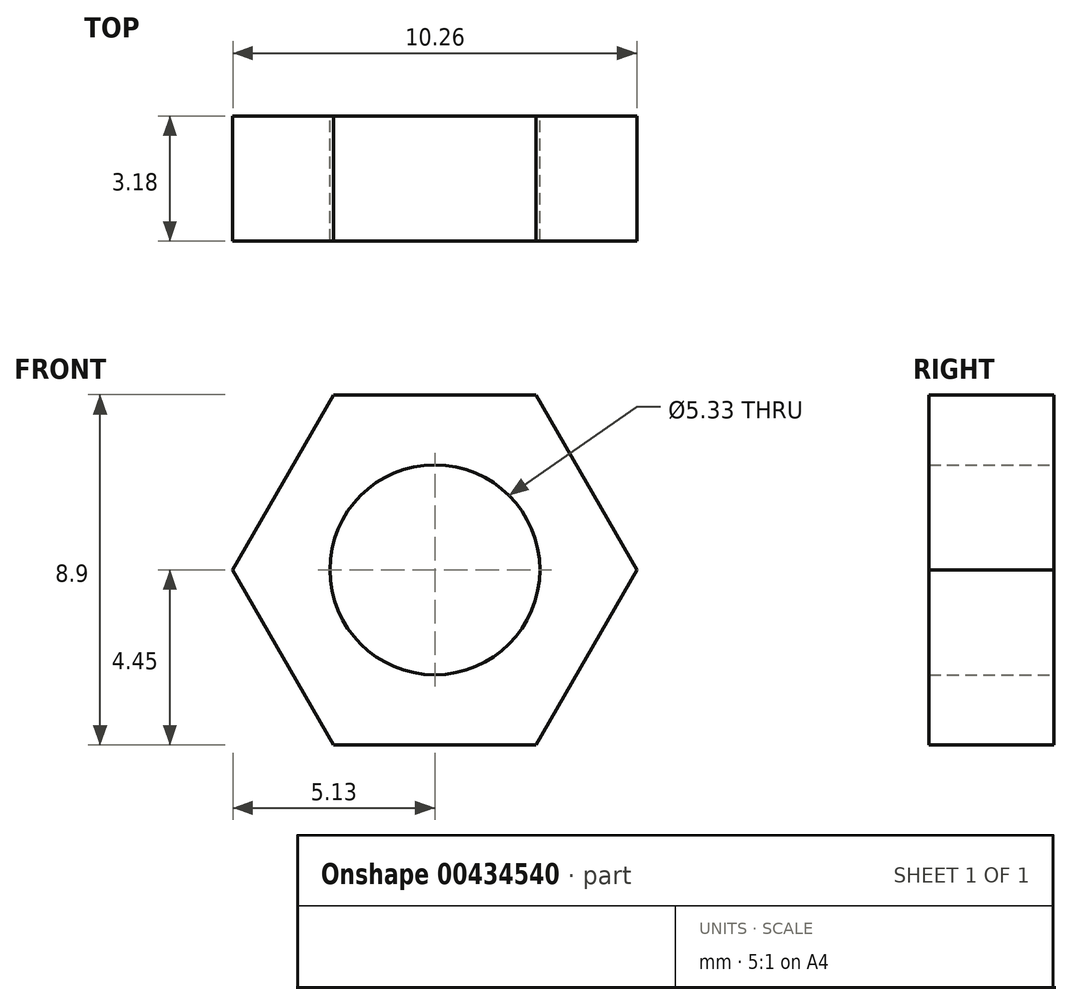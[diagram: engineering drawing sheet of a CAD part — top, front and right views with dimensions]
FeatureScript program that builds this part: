
annotation { "Feature Type Name" : "Feature", "Feature Type Description" : "" }
export const myFeature = defineFeature(function(context is Context, id is Id, definition is map)
    precondition{}
    {
        {
            var Q0;
            Q0=qCreatedBy(makeId("Front.planeOp"),FACE);
            var sketch = newSketch(context, id + "F0", { "sketchPlane" : qUnion([Q0])});
            skCircle(sketch, "E0.cCircle", {"center": v(0, 0) * mm, "radius": 4.45 * mm, "construction": true});
            skLineSegment(sketch, "E0.0", {"start": v(-2.57, 4.44) * mm, "end": v(2.57, 4.44) * mm});
            skLineSegment(sketch, "E0.1", {"start": v(2.57, 4.44) * mm, "end": v(5.13, 0) * mm});
            skLineSegment(sketch, "E0.2", {"start": v(5.13, 0) * mm, "end": v(2.57, -4.44) * mm});
            skLineSegment(sketch, "E0.3", {"start": v(2.57, -4.44) * mm, "end": v(-2.57, -4.45) * mm});
            skLineSegment(sketch, "E0.4", {"start": v(-2.57, -4.45) * mm, "end": v(-5.13, 0) * mm});
            skLineSegment(sketch, "E0.5", {"start": v(-5.13, 0) * mm, "end": v(-2.57, 4.44) * mm});
            skPoint(sketch, "E0.0.midPoint", {"position": v(0, 4.44) * mm});
            skCircle(sketch, "E1", {"center": v(0, 0) * mm, "radius": 2.67 * mm});
            skSolve(sketch);
        }
        {
            var Q0;
            Q0 = qSketchRegion(id + "F0", true);
            extrude(context, id + "F1", {"entities" : qUnion([Q0]), "depth" : 3.17 * mm});
        }
    });
